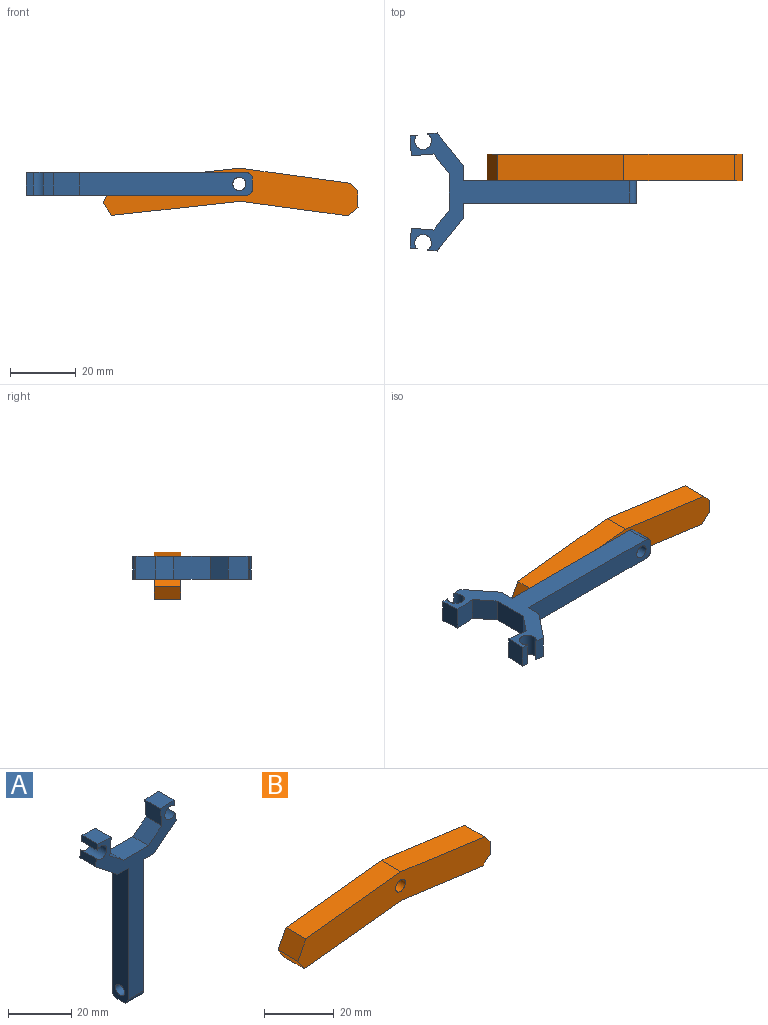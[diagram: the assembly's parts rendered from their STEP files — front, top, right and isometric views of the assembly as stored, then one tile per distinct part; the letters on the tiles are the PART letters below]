
ASSEMBLY  parts=2 mates=1
PART A: 25 faces, bbox 36x7x69 mm
  f0: plane 7x4.48mm, normal (0,0,-1), area 31.3mm2, adj f3,f17,f18,f19
  f1: plane 10.02x7.95mm, normal (-0.62,0,-0.78), area 89.5mm2, adj f2,f16,f17,f18
  f2: plane 7x4.48mm, normal (0,0,-1), area 31.3mm2, adj f1,f17,f18,f20
  f3: plane 10.02x7.95mm, normal (0.62,0,-0.78), area 89.5mm2, adj f0,f4,f17,f18
  f4: plane 7x2.95mm, normal (0.99,0,0.11), area 20.8mm2, adj f3,f5,f17,f18
  f5: cylinder r=2.55mm len=7mm, axis (0,1,0), area 88.5mm2, adj f4,f6,f17,f18
  f6: plane 7x2.21mm, normal (0.99,0,0.11), area 15.6mm2, adj f5,f7,f17,f18
  f7: plane 7x6.07mm, normal (-0.06,0,1), area 42.6mm2, adj f6,f8,f17,f18
  f8: plane 7x6.8mm, normal (-1,0,-0.08), area 47.8mm2, adj f7,f9,f17,f18
  f9: plane 7x5.96mm, normal (-0.62,0,0.78), area 53.3mm2, adj f8,f10,f17,f18
  f10: plane 11.27x7mm, normal (0,0,1), area 78.9mm2, adj f9,f11,f17,f18
  f11: plane 7x5.96mm, normal (0.62,0,0.78), area 53.3mm2, adj f10,f12,f17,f18
  f12: plane 7x6.8mm, normal (1,0,-0.08), area 47.8mm2, adj f11,f13,f17,f18
  f13: plane 7x6.07mm, normal (0.06,0,1), area 42.6mm2, adj f12,f14,f17,f18
  f14: plane 7x2.21mm, normal (-0.99,0,0.11), area 15.6mm2, adj f13,f15,f17,f18
  f15: cylinder r=2.55mm len=7mm, axis (0,1,0), area 88.5mm2, adj f14,f16,f17,f18
  f16: plane 7x2.95mm, normal (-0.99,0,0.11), area 20.8mm2, adj f1,f15,f17,f18
  f17: plane 66.99x35.99mm, normal (0,-1,0), area 567.3mm2, adj f0,f1,f2,f3,f4,f5,f6,f7
  f18: plane 66.99x35.99mm, normal (0,1,0), area 567.3mm2, adj f0,f1,f2,f3,f4,f5,f6,f7
  f19: plane 52.76x7mm, normal (1,0,0), area 355.1mm2, adj f0,f17,f18,f21,f22,f23,f24
  f20: plane 52.76x7mm, normal (-1,0,0), area 355.1mm2, adj f2,f17,f18,f21,f22,f23,f24
  f21: plane 7x3mm, normal (0,0,-1), area 21mm2, adj f19,f20,f23,f24
  f22: cylinder r=2mm len=7mm, axis (1,0,0), area 88mm2, adj f19,f20
  f23: cylinder r=2mm len=7mm, axis (1,0,0), area 22mm2, adj f17,f19,f20,f21
  f24: cylinder r=2mm len=7mm, axis (-1,0,0), area 22mm2, adj f18,f19,f20,f21
PART B: 12 faces, bbox 77.7x8x14.5 mm
  f0: plane 8x6.21mm, normal (-0.88,0,0.47), area 56.1mm2, adj f6,f7,f8,f11
  f1: plane 39.21x8mm, normal (0.11,0,-0.99), area 315.5mm2, adj f2,f7,f8,f11
  f2: plane 32.81x8mm, normal (-0.13,0,-0.99), area 264.9mm2, adj f1,f7,f8,f10
  f3: plane 8x4.64mm, normal (1,0,0), area 37.1mm2, adj f7,f8,f9,f10
  f4: plane 33.69x8mm, normal (0.14,0,0.99), area 272.1mm2, adj f6,f7,f8,f9
  f5: cylinder r=2mm len=8mm, axis (0,1,0), area 100.5mm2, adj f7,f8
  f6: plane 38.41x8mm, normal (-0.11,0,0.99), area 309.2mm2, adj f0,f4,f7,f8
  f7: plane 77.67x14.53mm, normal (0,-1,0), area 745.9mm2, adj f0,f1,f2,f3,f4,f5,f6,f9
  f8: plane 77.67x14.53mm, normal (0,1,0), area 745.9mm2, adj f0,f1,f2,f3,f4,f5,f6,f9
  f9: plane 8x2.63mm, normal (0.75,0,0.66), area 27.9mm2, adj f3,f4,f7,f8
  f10: plane 8x3.01mm, normal (0.66,0,-0.75), area 32mm2, adj f2,f3,f7,f8
  f11: plane 8x3.88mm, normal (-0.83,0,-0.56), area 37.5mm2, adj f0,f1,f7,f8
PLACE A rot(axis=(-0.58,-0.58,0.58),120deg) t=(-55.14,-10.17,-3.65)mm
PLACE B t=(-0.66,1.33,9.72)mm
MATE cylindrical A.f22 <-> B.f5  axis (0,1,0) through (5.86,-6.67,-0.15)mm
